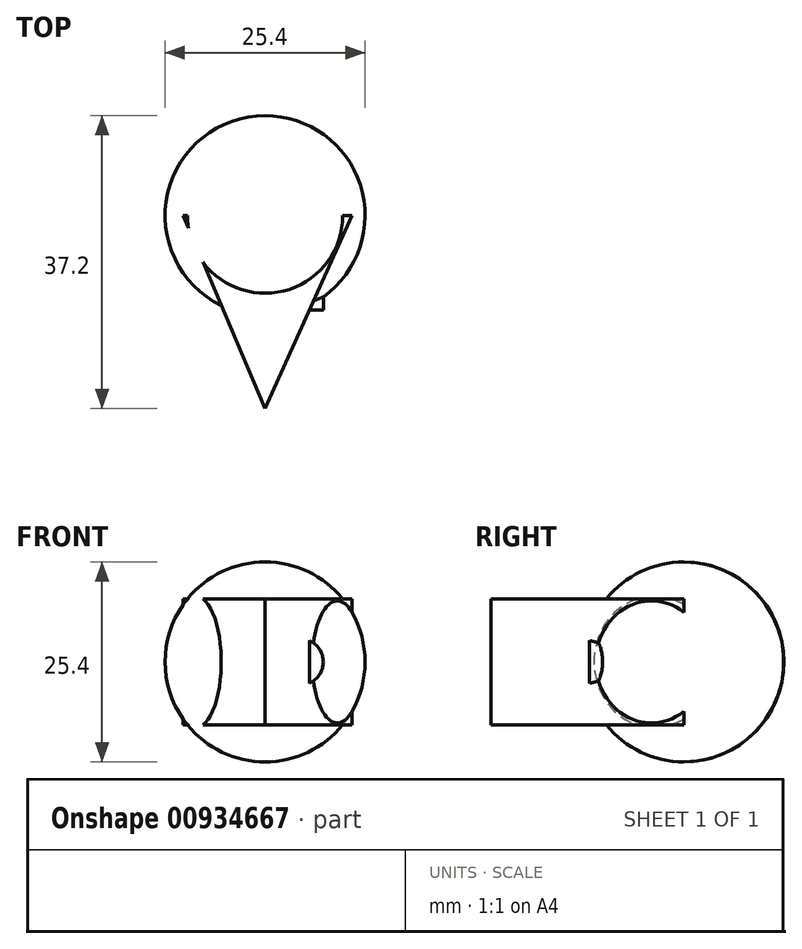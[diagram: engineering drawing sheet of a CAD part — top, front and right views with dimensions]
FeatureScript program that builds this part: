
annotation { "Feature Type Name" : "Feature", "Feature Type Description" : "" }
export const myFeature = defineFeature(function(context is Context, id is Id, definition is map)
    precondition{}
    {
        {
            var Q0;
            Q0=qCreatedBy(makeId("Front.planeOp"),FACE);
            var sketch = newSketch(context, id + "F0", { "sketchPlane" : qUnion([Q0])});
            skCircle(sketch, "E0", {"center": v(0, 0) * mm, "radius": 12.7 * mm});
            skLineSegment(sketch, "E1", {"start": v(0, 39.94) * mm, "end": v(0, -30.62) * mm});
            skSolve(sketch);
        }
        {
            var Q0;
            {var subQ0=sQuery(id+"F0.wireOp",EDGE,"E1");var subQ1=sQuery(id+"F0.wireOp",EDGE,"E0");var subQ2=makeQuery(id+"F0.imprint","INTERSECT",VERTEX,{"disambiguationData":[OD(0.0)],"derivedFrom":[subQ1,subQ0]});Q0=makeQuery(id+"F0.imprint","IMPRINT",FACE,{"disambiguationData":[TD([[makeQuery(id+"F0.imprint","IMPRINT",EDGE,{"disambiguationData":[TD([[subQ2,-1.0]])],"derivedFrom":subQ1}),1.0]])]});}
            var Q1;
            Q1=sQuery(id+"F0.wireOp",EDGE,"E1");
            revolve(context, id + "F1", {"surfaceOperationType" : NewSurfaceOperationType.NEW, "entities" : qUnion([Q0]), "axis" : qUnion([Q1]), "revolveType" : RevolveType.FULL});
        }
        {
            var Q0;
            Q0=qCreatedBy(makeId("Top.planeOp"),FACE);
            var sketch = newSketch(context, id + "F2", { "sketchPlane" : qUnion([Q0])});
            skLineSegment(sketch, "E2", {"start": v(0, 0) * mm, "end": v(11.03, 0) * mm});
            skLineSegment(sketch, "E3", {"start": v(11.03, 0) * mm, "end": v(-10.41, 0) * mm});
            skLineSegment(sketch, "E4", {"start": v(-10.41, 0) * mm, "end": v(0, -24.5) * mm});
            skLineSegment(sketch, "E5", {"start": v(0, -24.5) * mm, "end": v(11.03, 0) * mm});
            skSolve(sketch);
        }
        {
            var Q0;
            {var subQ2=sQuery(id+"F2.wireOp",EDGE,"E4");Q0=makeQuery(id+"F2.imprint","IMPRINT",FACE,{"disambiguationData":[TD([[makeQuery(id+"F2.imprint","IMPRINT",EDGE,{"derivedFrom":subQ2}),1.0]])]});}
            var Q1;
            Q1=sQuery(id+"F2.wireOp",EDGE,"E5");
            extrude(context, id + "F3", {"entities" : qUnion([Q0]), "operationType" : NewBodyOperationType.ADD, "surfaceEntities" : qUnion([Q1]), "depth" : 8 * mm, "offsetDistance" : 25 * mm});
        }
        {
            var Q0;
            Q0 = qSketchRegion(id + "F2", true);
            extrude(context, id + "F4", {"entities" : qUnion([Q0]), "operationType" : NewBodyOperationType.ADD, "oppositeDirection" : true, "depth" : 8 * mm, "offsetDistance" : 25 * mm});
        }
        {
            var Q0;
            Q0=qCreatedBy(makeId("Front.planeOp"),FACE);
            var sketch = newSketch(context, id + "F5", { "sketchPlane" : qUnion([Q0])});
            skCircle(sketch, "E6", {"center": v(4.44, 0) * mm, "radius": 2.96 * mm});
            skSolve(sketch);
        }
        {
            var Q0;
            Q0 = qSketchRegion(id + "F5", true);
            extrude(context, id + "F6", {"entities" : qUnion([Q0]), "operationType" : NewBodyOperationType.ADD, "depth" : 12 * mm, "offsetDistance" : 25 * mm});
        }
    });
